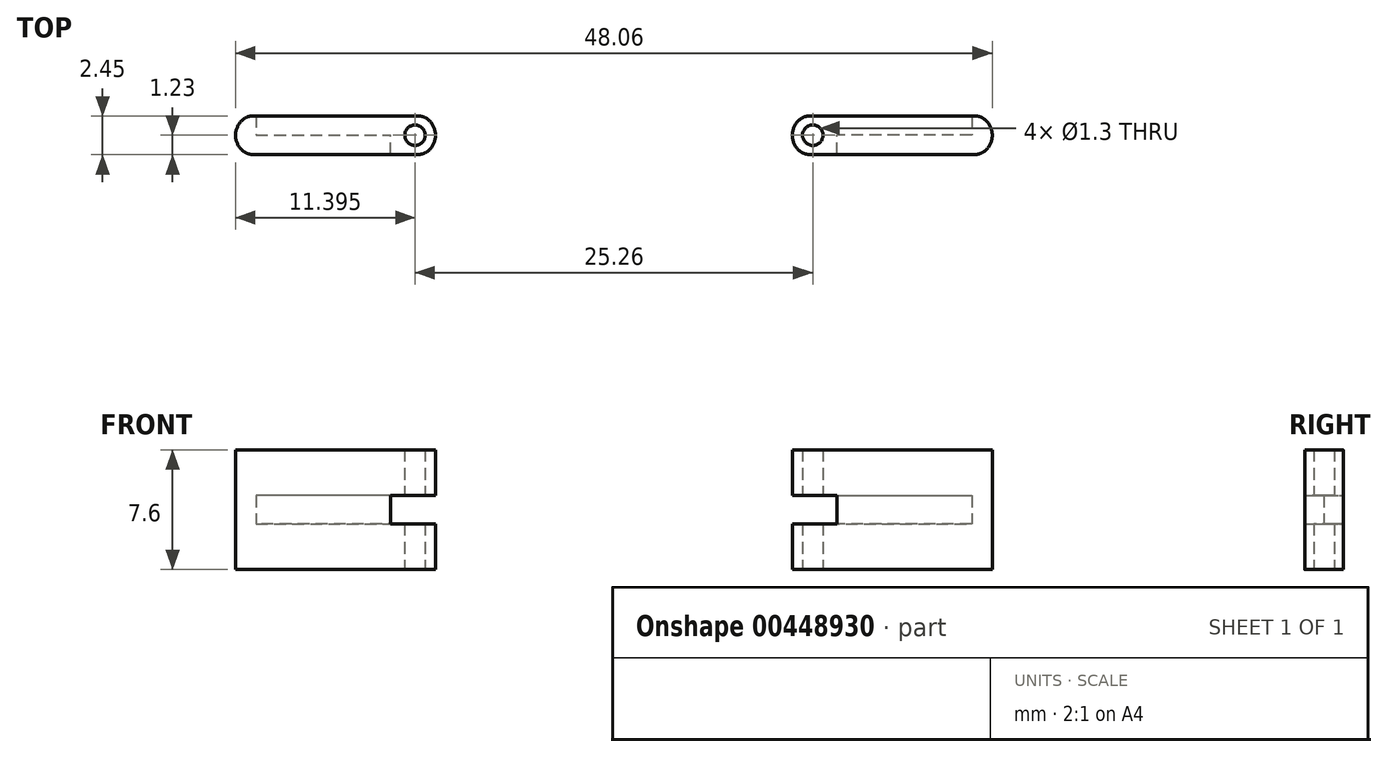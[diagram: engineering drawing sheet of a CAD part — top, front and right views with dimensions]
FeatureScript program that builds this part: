
annotation { "Feature Type Name" : "Feature", "Feature Type Description" : "" }
export const myFeature = defineFeature(function(context is Context, id is Id, definition is map)
    precondition{}
    {
        {
            var Q0;
            Q0=qCreatedBy(makeId("Top.planeOp"),FACE);
            var sketch = newSketch(context, id + "F0", { "sketchPlane" : qUnion([Q0])});
            skPoint(sketch, "E0.endSnap0", {"position": v(8.6, 0) * mm});
            skLineSegment(sketch, "E1", {"start": v(8.6, -1.83) * mm, "end": v(8.56, -1.83) * mm});
            skLineSegment(sketch, "E2", {"start": v(7.7, -3.06) * mm, "end": v(4.3, -3.06) * mm});
            skArc(sketch, "E3", {"start": v(7.7, -3.06) * mm, "mid": v(8.56, -1.83) * mm, "end": v(7.7, -0.6) * mm});
            skLineSegment(sketch, "E4", {"start": v(7.7, -0.6) * mm, "end": v(1.5, -0.6) * mm});
            skCircle(sketch, "E5", {"center": v(7.26, -1.83) * mm, "radius": 0.65 * mm});
            skLineSegment(sketch, "E6", {"start": v(-3.28, -3.06) * mm, "end": v(4.3, -3.06) * mm});
            skPoint(sketch, "E7.end.orphan", {"position": v(-4.14, -3.06) * mm});
            skLineSegment(sketch, "E8", {"start": v(1.5, -0.6) * mm, "end": v(-3.28, -0.6) * mm});
            skArc(sketch, "E9.trimOffspring", {"start": v(-3.28, -0.6) * mm, "mid": v(-4.14, -1.83) * mm, "end": v(-3.28, -3.06) * mm});
            skLineSegment(sketch, "E10", {"start": v(-2.84, -1.83) * mm, "end": v(-2.84, -0.6) * mm});
            skLineSegment(sketch, "E11", {"start": v(5.7, -1.83) * mm, "end": v(5.7, -3.06) * mm});
            skLineSegment(sketch, "E12.trimOffspring", {"start": v(5.7, -1.83) * mm, "end": v(-2.84, -1.83) * mm});
            skSolve(sketch);
        }
        {
            var Q0;
            Q0 = qSketchRegion(id + "F0", true);
            extrude(context, id + "F1", {"entities" : qUnion([Q0]), "depth" : 2.9 * mm});
        }
        {
            var Q0;
            {var subQ3=sQuery(id+"F0.wireOp",EDGE,"E6");Q0=makeQuery(id+"F0.imprint","IMPRINT",FACE,{"disambiguationData":[TD([[makeQuery(id+"F0.imprint","IMPRINT",EDGE,{"derivedFrom":subQ3}),1.0]])]});}
            extrude(context, id + "F2", {"entities" : qUnion([Q0]), "operationType" : NewBodyOperationType.ADD, "depth" : 4.7 * mm});
        }
        {
            var Q0;
            Q0=makeQuery(id+"F2.opExtrude","CAP_FACE",FACE,{"disambiguationData":[OSD([sQuery(id+"F0.wireOp",EDGE,"E2"),sQuery(id+"F0.wireOp",EDGE,"E6"),sQuery(id+"F0.wireOp",EDGE,"E8"),sQuery(id+"F0.wireOp",EDGE,"E9.trimOffspring"),sQuery(id+"F0.wireOp",EDGE,"E10"),sQuery(id+"F0.wireOp",EDGE,"E11"),sQuery(id+"F0.wireOp",EDGE,"E12.trimOffspring")])],"isStart":false});
            var sketch = newSketch(context, id + "F3", { "sketchPlane" : qUnion([Q0])});
            skLineSegment(sketch, "E13.0.0", {"start": v(7.7, -0.6) * mm, "end": v(-2.84, -0.6) * mm});
            skLineSegment(sketch, "E13.0.1", {"start": v(-2.84, -0.6) * mm, "end": v(-2.84, -1.83) * mm});
            skLineSegment(sketch, "E13.0.2", {"start": v(-2.84, -1.83) * mm, "end": v(5.7, -1.83) * mm});
            skLineSegment(sketch, "E13.0.3", {"start": v(5.7, -1.83) * mm, "end": v(5.7, -3.06) * mm});
            skLineSegment(sketch, "E13.0.4", {"start": v(5.7, -3.06) * mm, "end": v(7.7, -3.06) * mm});
            skArc(sketch, "E13.0.5", {"start": v(7.7, -3.06) * mm, "mid": v(8.56, -1.83) * mm, "end": v(7.7, -0.6) * mm});
            skLineSegment(sketch, "E14.0.0", {"start": v(-2.84, -1.83) * mm, "end": v(-2.84, -0.6) * mm});
            skLineSegment(sketch, "E14.0.1", {"start": v(-2.84, -0.6) * mm, "end": v(-3.28, -0.6) * mm});
            skArc(sketch, "E14.0.2", {"start": v(-3.28, -0.6) * mm, "mid": v(-4.14, -1.83) * mm, "end": v(-3.28, -3.06) * mm});
            skLineSegment(sketch, "E14.0.3", {"start": v(-3.28, -3.06) * mm, "end": v(5.7, -3.06) * mm});
            skLineSegment(sketch, "E14.0.4", {"start": v(5.7, -3.06) * mm, "end": v(5.7, -1.83) * mm});
            skLineSegment(sketch, "E14.0.5", {"start": v(5.7, -1.83) * mm, "end": v(-2.84, -1.83) * mm});
            skCircle(sketch, "E15.0", {"center": v(7.26, -1.83) * mm, "radius": 0.65 * mm});
            skSolve(sketch);
        }
        {
            var Q0;
            Q0 = qSketchRegion(id + "F3", true);
            extrude(context, id + "F4", {"entities" : qUnion([Q0]), "operationType" : NewBodyOperationType.ADD, "depth" : 2.9 * mm});
        }
        {
            var Q0;
            Q0=makeQuery(id+"F4.opExtrude","SWEPT_EDGE",EDGE,{"disambiguationData":[OSD([sQuery(id+"F3.wireOp",EDGE,"E13.0.0"),sQuery(id+"F3.wireOp",EDGE,"E13.0.5")])]});
            var Q1;
            Q1=makeQuery(id+"F1.opExtrude","SWEPT_EDGE",EDGE,{"disambiguationData":[OSD([sQuery(id+"F0.wireOp",EDGE,"E3"),sQuery(id+"F0.wireOp",EDGE,"E4")])]});
            var Q2;
            {var subQ0=sQuery(id+"F0.wireOp",EDGE,"E9.trimOffspring");var subQ1=sQuery(id+"F0.wireOp",EDGE,"E8");Q2=makeQuery(id+"F4.boolean.opBoolean","MERGE",EDGE,{"derivedFrom":[makeQuery(id+"F2.boolean.opBoolean","MERGE",EDGE,{"derivedFrom":[makeQuery(id+"F1.opExtrude","SWEPT_EDGE",EDGE,{"disambiguationData":[OSD([subQ1,subQ0])]}),makeQuery(id+"F2.opExtrude","SWEPT_EDGE",EDGE,{"disambiguationData":[OSD([subQ1,subQ0])]})]}),makeQuery(id+"F4.opExtrude","SWEPT_EDGE",EDGE,{"disambiguationData":[OSD([sQuery(id+"F3.wireOp",EDGE,"E14.0.1"),sQuery(id+"F3.wireOp",EDGE,"E14.0.2")])]})]});}
            var Q3;
            Q3=makeQuery(id+"F4.opExtrude","SWEPT_EDGE",EDGE,{"disambiguationData":[OSD([sQuery(id+"F3.wireOp",EDGE,"E13.0.4"),sQuery(id+"F3.wireOp",EDGE,"E13.0.5")])]});
            var Q4;
            {var subQ0=sQuery(id+"F0.wireOp",EDGE,"E9.trimOffspring");var subQ1=sQuery(id+"F0.wireOp",EDGE,"E6");Q4=makeQuery(id+"F4.boolean.opBoolean","MERGE",EDGE,{"derivedFrom":[makeQuery(id+"F2.boolean.opBoolean","MERGE",EDGE,{"derivedFrom":[makeQuery(id+"F1.opExtrude","SWEPT_EDGE",EDGE,{"disambiguationData":[OSD([subQ1,subQ0])]}),makeQuery(id+"F2.opExtrude","SWEPT_EDGE",EDGE,{"disambiguationData":[OSD([subQ1,subQ0])]})]}),makeQuery(id+"F4.opExtrude","SWEPT_EDGE",EDGE,{"disambiguationData":[OSD([sQuery(id+"F3.wireOp",EDGE,"E14.0.2"),sQuery(id+"F3.wireOp",EDGE,"E14.0.3")])]})]});}
            var Q5;
            Q5=makeQuery(id+"F1.opExtrude","SWEPT_EDGE",EDGE,{"disambiguationData":[OSD([sQuery(id+"F0.wireOp",EDGE,"E2"),sQuery(id+"F0.wireOp",EDGE,"E3")])]});
            fillet(context, id + "F5", {"entities" : qUnion([Q0, Q1, Q2, Q3, Q4, Q5]), "radius" : 1 * mm, "tangentPropagation" : true, "allowEdgeOverflow" : false});
        }
        {
            var Q0;
            Q0=qCreatedBy(makeId("Top.planeOp"),FACE);
            var sketch = newSketch(context, id + "F6", { "sketchPlane" : qUnion([Q0])});
            skLineSegment(sketch, "E16", {"start": v(13.63, -1.65) * mm, "end": v(19.89, -1.65) * mm});
            skSolve(sketch);
        }
        {
            var Q0;
            Q0=sQuery(id+"F6.wireOp",VERTEX,"E16.end");
            var Q1;
            Q1=sQuery(id+"F6.wireOp",EDGE,"E16");
            cPlane(context, id + "F7", {"entities" : qUnion([Q0, Q1]), "cplaneType" : CPlaneType.LINE_POINT, "offset" : 25 * mm, "width" : 150 * mm, "height" : 150 * mm});
        }
        {
            var Q0;
            Q0=makeQuery(id+"F1.opExtrude","SWEPT_BODY",BODY,{"disambiguationData":[OSD([sQuery(id+"F0.wireOp",EDGE,"E2"),sQuery(id+"F0.wireOp",EDGE,"E3"),sQuery(id+"F0.wireOp",EDGE,"E4"),sQuery(id+"F0.wireOp",EDGE,"E5"),sQuery(id+"F0.wireOp",EDGE,"E6"),sQuery(id+"F0.wireOp",EDGE,"E8"),sQuery(id+"F0.wireOp",EDGE,"E9.trimOffspring")])]});
            var Q1;
            Q1=qCreatedBy(id+"F7.planeOp",FACE);
            mirror(context, id + "F8", {"entities" : qUnion([Q0]), "mirrorPlane" : qUnion([Q1])});
        }
    });
